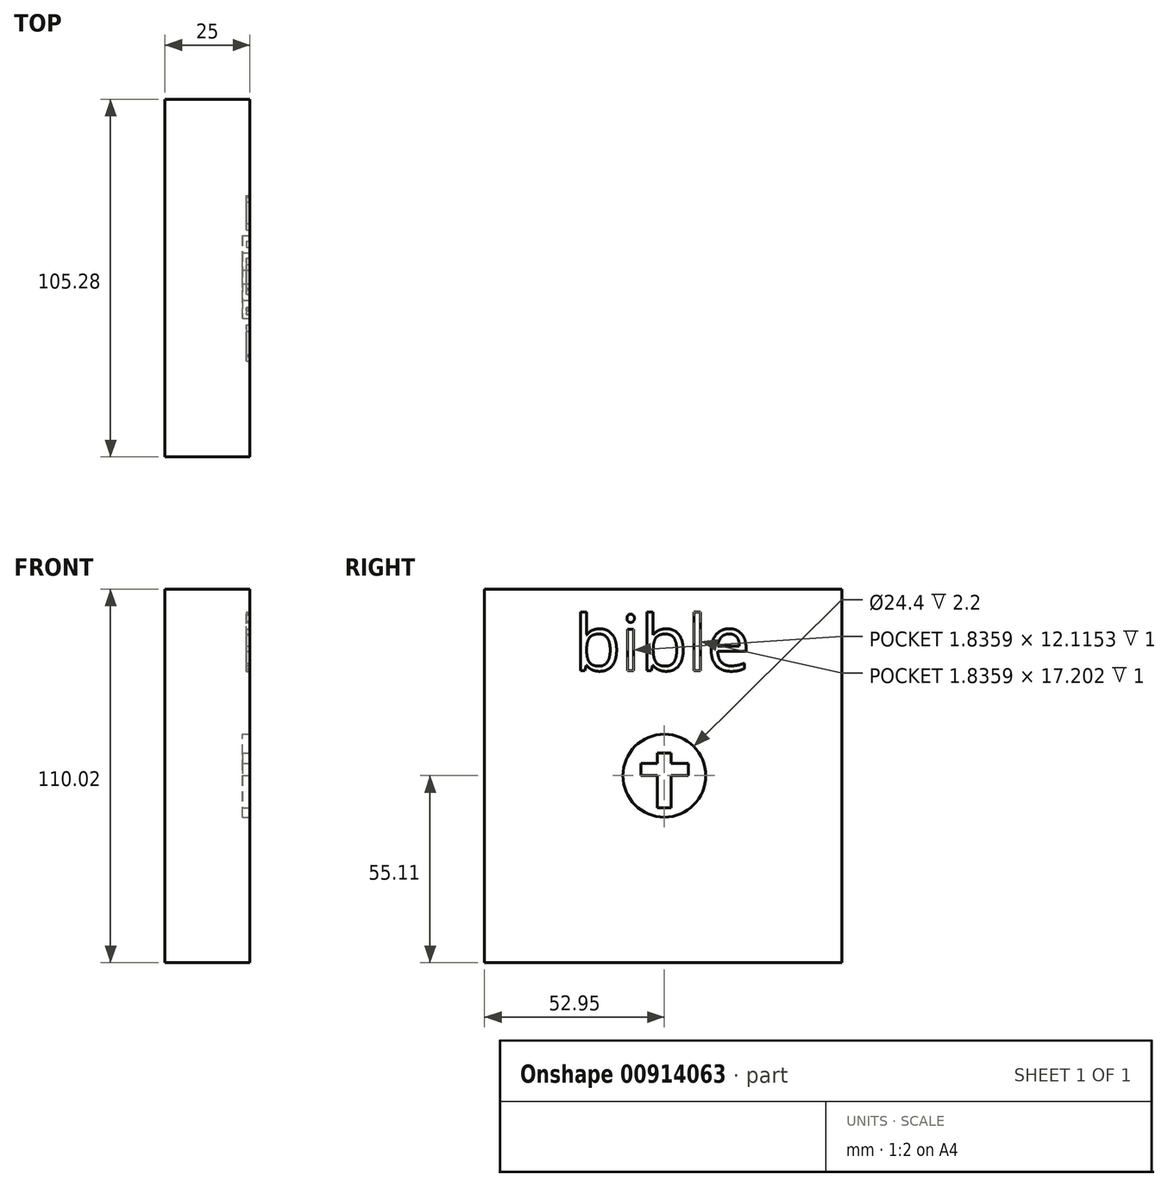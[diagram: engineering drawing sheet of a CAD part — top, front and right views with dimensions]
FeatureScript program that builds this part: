
annotation { "Feature Type Name" : "Feature", "Feature Type Description" : "" }
export const myFeature = defineFeature(function(context is Context, id is Id, definition is map)
    precondition{}
    {
        {
            var Q0;
            Q0=qCreatedBy(makeId("Right.planeOp"),FACE);
            var sketch = newSketch(context, id + "F0", { "sketchPlane" : qUnion([Q0])});
            skLineSegment(sketch, "E0.bottom", {"start": v(-52.95, 54.9) * mm, "end": v(52.33, 54.9) * mm});
            skLineSegment(sketch, "E0.top", {"start": v(-52.95, -55.11) * mm, "end": v(52.33, -55.11) * mm});
            skLineSegment(sketch, "E0.left", {"start": v(-52.95, 54.9) * mm, "end": v(-52.95, -55.11) * mm});
            skLineSegment(sketch, "E0.right", {"start": v(52.33, 54.9) * mm, "end": v(52.33, -55.11) * mm});
            skSolve(sketch);
        }
        {
            var Q0;
            Q0=makeQuery(id+"F0.imprint","IMPRINT",FACE,{"disambiguationData":[TD([[makeQuery(id+"F0.imprint","IMPRINT",EDGE,{"derivedFrom":sQuery(id+"F0.wireOp",EDGE,"E0.bottom")}),-1.0]])]});
            extrude(context, id + "F1", {"entities" : qUnion([Q0]), "endBound" : BoundingType.SYMMETRIC, "depth" : 25 * mm, "offsetDistance" : 25 * mm});
        }
        {
            var Q0;
            Q0=makeQuery(id+"F1.opExtrude","CAP_FACE",FACE,{"disambiguationData":[OSD([sQuery(id+"F0.wireOp",EDGE,"E0.bottom"),sQuery(id+"F0.wireOp",EDGE,"E0.top"),sQuery(id+"F0.wireOp",EDGE,"E0.left"),sQuery(id+"F0.wireOp",EDGE,"E0.right")])],"isStart":false});
            cPlane(context, id + "F2", {"entities" : qUnion([Q0]), "cplaneType" : CPlaneType.OFFSET, "offset" : 25 * mm, "width" : 150 * mm, "height" : 150 * mm});
        }
        {
            var Q0;
            Q0=qCreatedBy(id+"F2.planeOp",FACE);
            var sketch = newSketch(context, id + "F3", { "sketchPlane" : qUnion([Q0])});
            skCircle(sketch, "E1", {"center": v(0, 0) * mm, "radius": 12.2 * mm});
            skLineSegment(sketch, "E2.bottom", {"start": v(-2.04, 6.7) * mm, "end": v(2.04, 6.7) * mm});
            skLineSegment(sketch, "E2.top", {"start": v(-2.04, -9.4) * mm, "end": v(2.04, -9.4) * mm});
            skLineSegment(sketch, "E2.left", {"start": v(-2.04, 6.7) * mm, "end": v(-2.04, -9.4) * mm});
            skLineSegment(sketch, "E2.right", {"start": v(2.04, 6.7) * mm, "end": v(2.04, -9.4) * mm});
            skLineSegment(sketch, "E3.bottom", {"start": v(-6.89, 3.59) * mm, "end": v(7.08, 3.59) * mm});
            skLineSegment(sketch, "E3.top", {"start": v(-6.89, 0) * mm, "end": v(7.08, 0) * mm});
            skLineSegment(sketch, "E3.left", {"start": v(-6.89, 3.59) * mm, "end": v(-6.89, 0) * mm});
            skLineSegment(sketch, "E3.right", {"start": v(7.08, 3.59) * mm, "end": v(7.08, 0) * mm});
            skSolve(sketch);
        }
        {
            var Q0;
            Q0=makeQuery(id+"F3.imprint","IMPRINT",FACE,{"disambiguationData":[TD([[makeQuery(id+"F3.imprint","IMPRINT",EDGE,{"derivedFrom":sQuery(id+"F3.wireOp",EDGE,"E1")}),1.0]])]});
            extrude(context, id + "F4", {"entities" : qUnion([Q0]), "operationType" : NewBodyOperationType.REMOVE, "oppositeDirection" : true, "depth" : 27.2 * mm, "offsetDistance" : 25 * mm});
        }
        {
            var Q0;
            Q0=qCreatedBy(id+"F2.planeOp",FACE);
            var sketch = newSketch(context, id + "F5", { "sketchPlane" : qUnion([Q0])});
            skText(sketch, "E4", { "text": "bible", "fontName": "OpenSans-Regular.ttf"});
            const initialGuessF5  = {"E4": [-0.02667, 0.03094, 1, 0, 0.0163]};
            skSetInitialGuess(sketch, initialGuessF5);
            skSolve(sketch);
        }
        {
            var Q0;
            Q0 = qSketchRegion(id + "F5", true);
            extrude(context, id + "F6", {"entities" : qUnion([Q0]), "operationType" : NewBodyOperationType.REMOVE, "oppositeDirection" : true, "depth" : 26 * mm, "offsetDistance" : 25 * mm});
        }
    });
